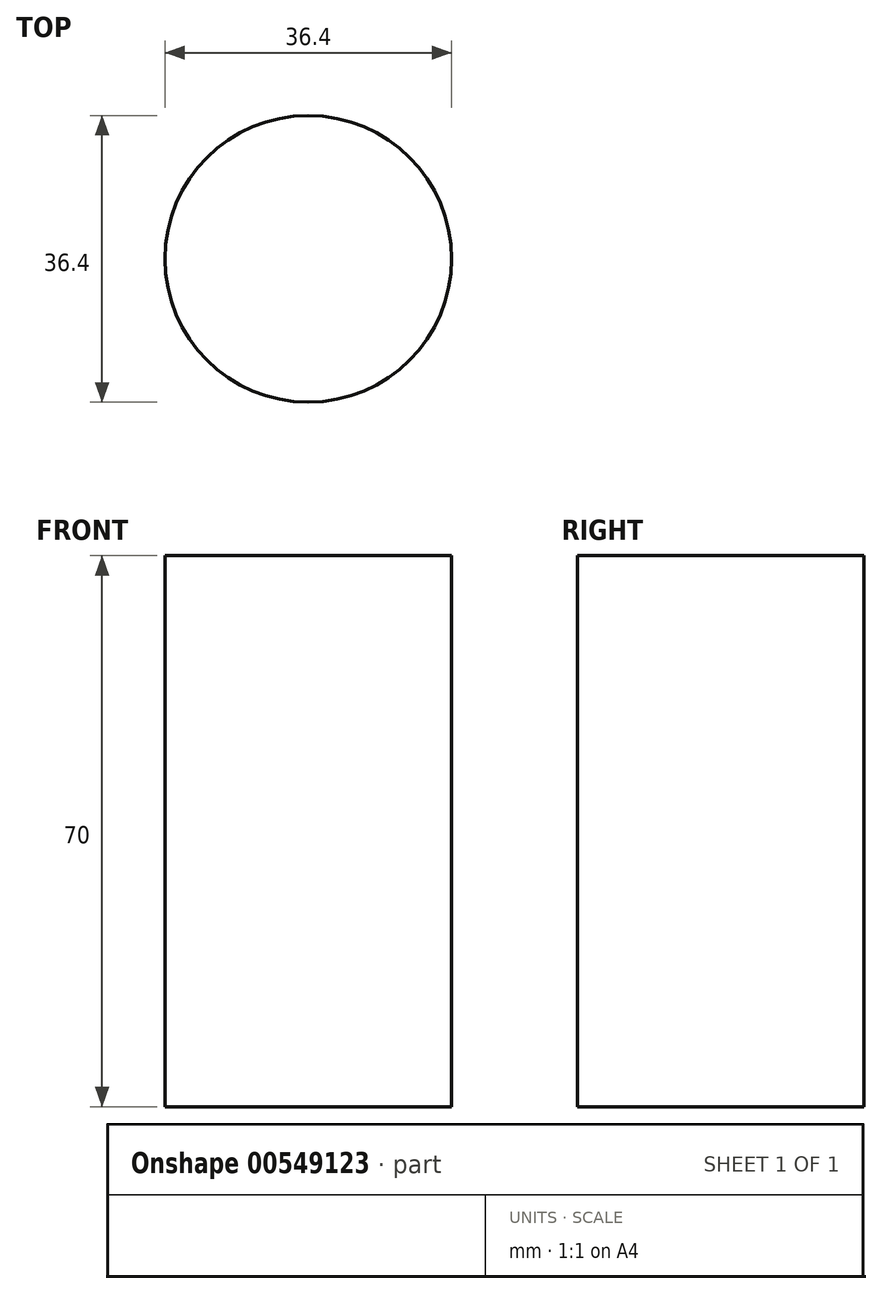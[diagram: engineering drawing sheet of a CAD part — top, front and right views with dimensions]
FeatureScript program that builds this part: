
annotation { "Feature Type Name" : "Feature", "Feature Type Description" : "" }
export const myFeature = defineFeature(function(context is Context, id is Id, definition is map)
    precondition{}
    {
        {
            var Q0;
            Q0=qCreatedBy(makeId("Top.planeOp"),FACE);
            var sketch = newSketch(context, id + "F0", { "sketchPlane" : qUnion([Q0])});
            skCircle(sketch, "E0", {"center": v(0, 0) * mm, "radius": 18.2 * mm});
            skSolve(sketch);
        }
        {
            var Q0;
            Q0=makeQuery(id+"F0.imprint","IMPRINT",FACE,{"disambiguationData":[TD([[makeQuery(id+"F0.imprint","IMPRINT",EDGE,{"derivedFrom":sQuery(id+"F0.wireOp",EDGE,"E0")}),1.0]])]});
            extrude(context, id + "F1", {"entities" : qUnion([Q0]), "depth" : 70 * mm, "offsetDistance" : 25 * mm});
        }
    });
